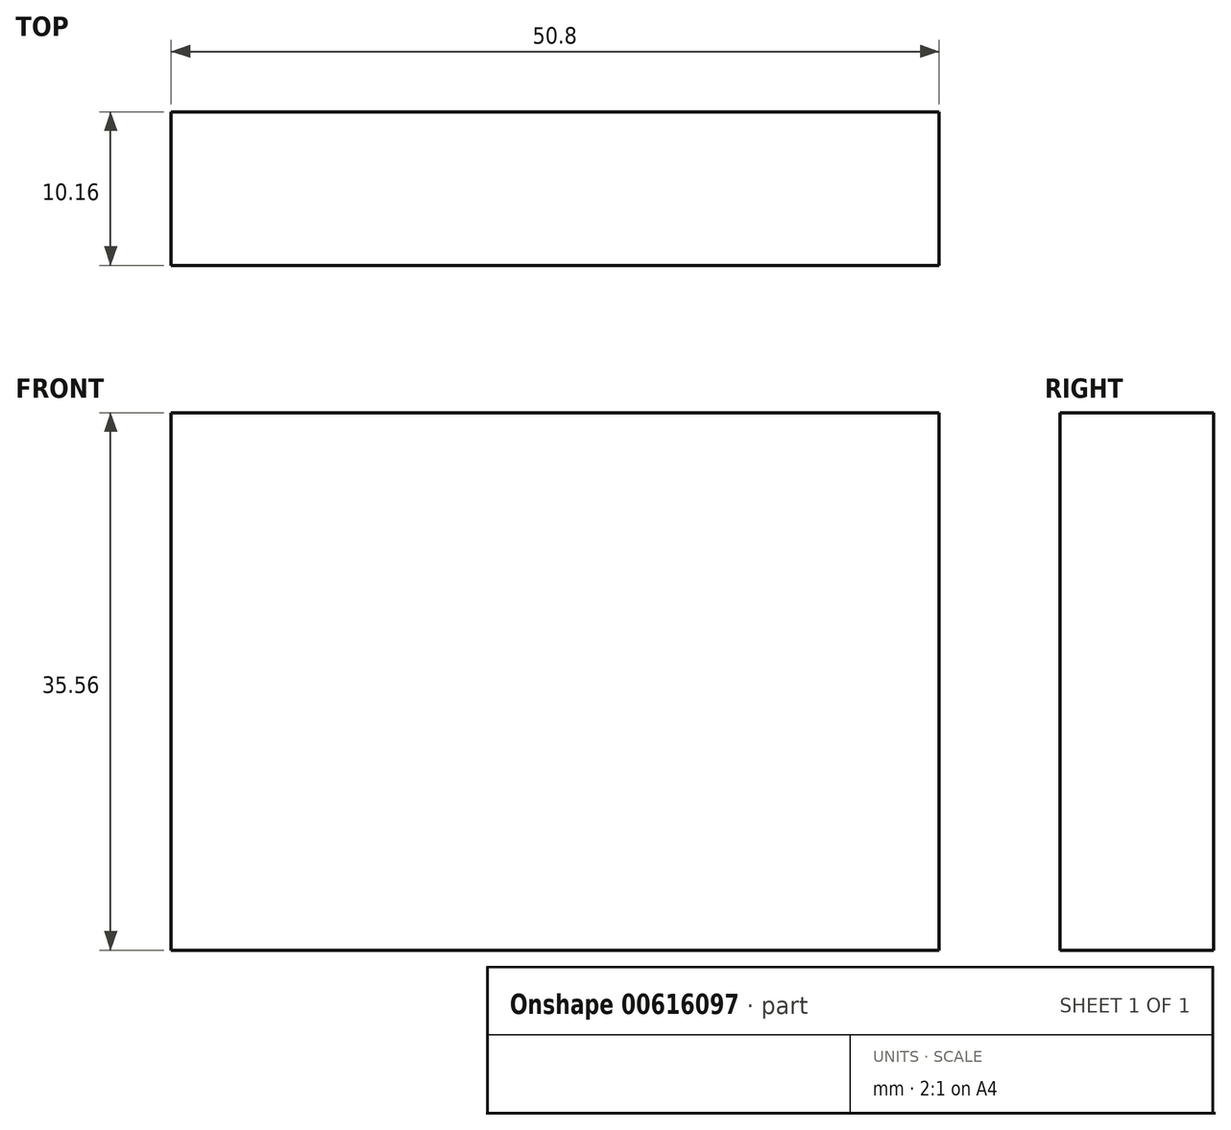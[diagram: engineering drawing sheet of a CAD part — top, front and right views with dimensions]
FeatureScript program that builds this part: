
annotation { "Feature Type Name" : "Feature", "Feature Type Description" : "" }
export const myFeature = defineFeature(function(context is Context, id is Id, definition is map)
    precondition{}
    {
        {
            var Q0;
            Q0=qCreatedBy(makeId("Front.planeOp"),FACE);
            var sketch = newSketch(context, id + "F0", { "sketchPlane" : qUnion([Q0])});
            skLineSegment(sketch, "E0.bottom", {"start": v(0, 0) * mm, "end": v(-50.8, 0) * mm});
            skLineSegment(sketch, "E0.top", {"start": v(0, 35.56) * mm, "end": v(-50.8, 35.56) * mm});
            skLineSegment(sketch, "E0.left", {"start": v(0, 0) * mm, "end": v(0, 35.56) * mm});
            skLineSegment(sketch, "E0.right", {"start": v(-50.8, 0) * mm, "end": v(-50.8, 35.56) * mm});
            skSolve(sketch);
        }
        {
            var Q0;
            Q0=makeQuery(id+"F0.imprint","IMPRINT",FACE,{"disambiguationData":[TD([[makeQuery(id+"F0.imprint","IMPRINT",EDGE,{"derivedFrom":sQuery(id+"F0.wireOp",EDGE,"E0.bottom")}),-1.0]])]});
            extrude(context, id + "F1", {"entities" : qUnion([Q0]), "depth" : 10.16 * mm, "offsetDistance" : 25.4 * mm});
        }
    });
